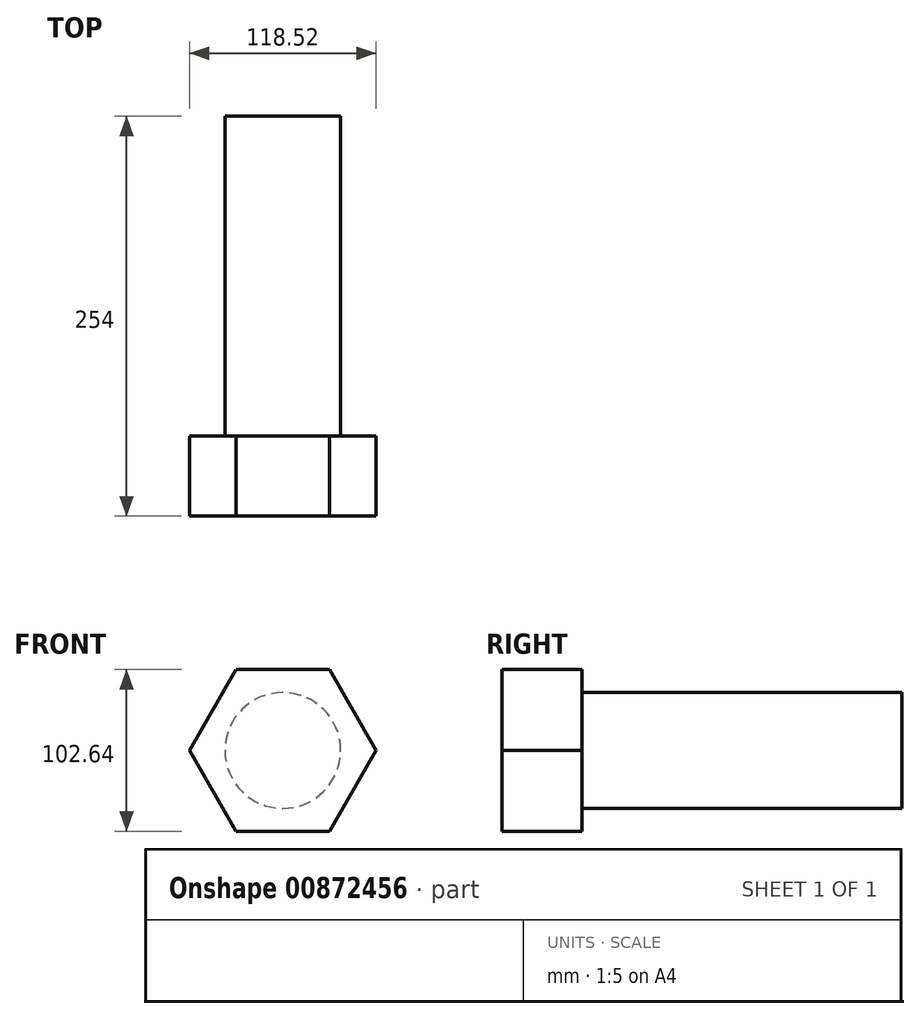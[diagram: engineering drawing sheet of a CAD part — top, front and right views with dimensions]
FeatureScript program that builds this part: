
annotation { "Feature Type Name" : "Feature", "Feature Type Description" : "" }
export const myFeature = defineFeature(function(context is Context, id is Id, definition is map)
    precondition{}
    {
        {
            var Q0;
            Q0=qCreatedBy(makeId("Front.planeOp"),FACE);
            var sketch = newSketch(context, id + "F0", { "sketchPlane" : qUnion([Q0])});
            skCircle(sketch, "E0.cCircle", {"center": v(0, 0) * mm, "radius": 51.32 * mm, "construction": true});
            skLineSegment(sketch, "E0.0", {"start": v(29.63, -51.32) * mm, "end": v(-29.63, -51.32) * mm});
            skLineSegment(sketch, "E0.1", {"start": v(-29.63, -51.32) * mm, "end": v(-59.26, 0) * mm});
            skLineSegment(sketch, "E0.2", {"start": v(-59.26, 0) * mm, "end": v(-29.63, 51.32) * mm});
            skLineSegment(sketch, "E0.3", {"start": v(-29.63, 51.32) * mm, "end": v(29.63, 51.32) * mm});
            skLineSegment(sketch, "E0.4", {"start": v(29.63, 51.32) * mm, "end": v(59.26, 0) * mm});
            skLineSegment(sketch, "E0.5", {"start": v(59.26, 0) * mm, "end": v(29.63, -51.32) * mm});
            skPoint(sketch, "E0.0.midPoint", {"position": v(0, -51.32) * mm});
            skSolve(sketch);
        }
        {
            var Q0;
            Q0=qSketchRegion(id+"F0",true);
            extrude(context, id + "F1", {"entities" : qUnion([Q0]), "depth" : 50.8 * mm, "offsetDistance" : 25.4 * mm});
        }
        {
            var Q0;
            Q0=makeQuery(id+"F1.opExtrude","CAP_FACE",FACE,{"disambiguationData":[OSD([sQuery(id+"F0.wireOp",EDGE,"E0.0"),sQuery(id+"F0.wireOp",EDGE,"E0.1"),sQuery(id+"F0.wireOp",EDGE,"E0.2"),sQuery(id+"F0.wireOp",EDGE,"E0.3"),sQuery(id+"F0.wireOp",EDGE,"E0.4"),sQuery(id+"F0.wireOp",EDGE,"E0.5")])],"isStart":true});
            var sketch = newSketch(context, id + "F2", { "sketchPlane" : qUnion([Q0])});
            skCircle(sketch, "E1", {"center": v(0, 0) * mm, "radius": 36.74 * mm});
            skSolve(sketch);
        }
        {
            var Q0;
            Q0=qSketchRegion(id+"F2",true);
            extrude(context, id + "F3", {"entities" : qUnion([Q0]), "operationType" : NewBodyOperationType.ADD, "depth" : 203.2 * mm, "offsetDistance" : 25.4 * mm});
        }
    });
